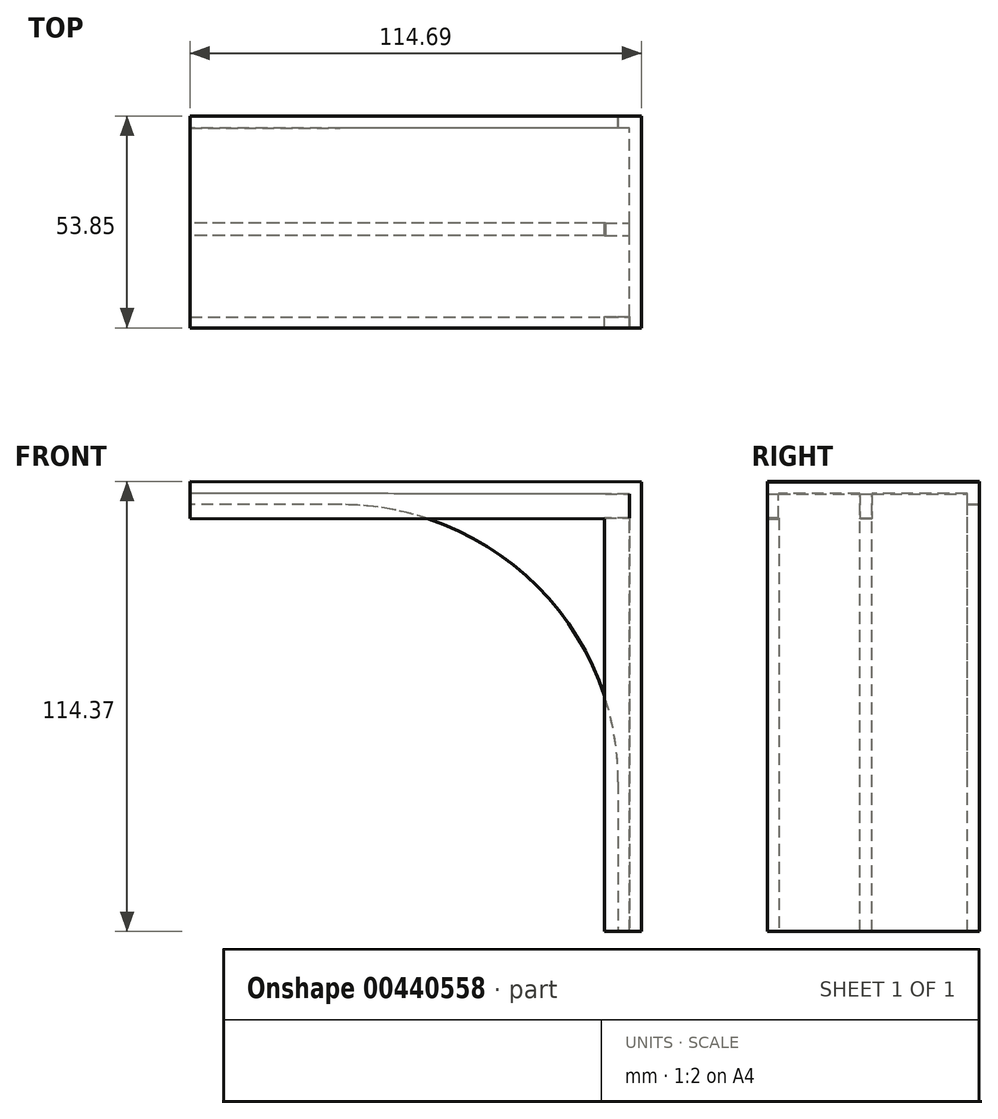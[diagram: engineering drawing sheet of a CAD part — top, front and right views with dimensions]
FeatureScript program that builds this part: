
annotation { "Feature Type Name" : "Feature", "Feature Type Description" : "" }
export const myFeature = defineFeature(function(context is Context, id is Id, definition is map)
    precondition{}
    {
        {
            var Q0;
            Q0=qCreatedBy(makeId("Front.planeOp"),FACE);
            var sketch = newSketch(context, id + "F0", { "sketchPlane" : qUnion([Q0])});
            skLineSegment(sketch, "E0", {"start": v(-76.07, 76.33) * mm, "end": v(76.59, -75.81) * mm});
            skLineSegment(sketch, "E1", {"start": v(76.59, -75.81) * mm, "end": v(76.59, 76.07) * mm});
            skLineSegment(sketch, "E2", {"start": v(76.59, 76.07) * mm, "end": v(-76.07, 76.33) * mm});
            skLineSegment(sketch, "E3.0", {"start": v(73.54, 73.03) * mm, "end": v(-76.08, 73.28) * mm});
            skLineSegment(sketch, "E3.1", {"start": v(73.54, -75.81) * mm, "end": v(73.54, 73.03) * mm});
            skSolve(sketch);
        }
        {
            var Q0;
            {var subQ1=sQuery(id+"F0.wireOp",EDGE,"E1");Q0=makeQuery(id+"F0.imprint","IMPRINT",FACE,{"disambiguationData":[TD([[makeQuery(id+"F0.imprint","IMPRINT",EDGE,{"derivedFrom":subQ1}),1.0]])]});}
            extrude(context, id + "F1", {"entities" : qUnion([Q0]), "depth" : 38.1 * mm});
        }
        {
            var Q0;
            {var subQ0=sQuery(id+"F0.wireOp",EDGE,"E3.0");var subQ1=sQuery(id+"F0.wireOp",EDGE,"E0");var subQ2=makeQuery(id+"F0.imprint","INTERSECT",VERTEX,{"derivedFrom":[subQ1,subQ0]});Q0=makeQuery(id+"F0.imprint","IMPRINT",FACE,{"disambiguationData":[TD([[makeQuery(id+"F0.imprint","IMPRINT",EDGE,{"disambiguationData":[TD([[subQ2,-1.0]])],"derivedFrom":subQ1}),1.0]])]});}
            extrude(context, id + "F2", {"entities" : qUnion([Q0]), "operationType" : NewBodyOperationType.ADD, "depth" : 3.05 * mm});
        }
        {
            var Q0;
            {var subQ0=sQuery(id+"F0.wireOp",EDGE,"E3.1");var subQ1=sQuery(id+"F0.wireOp",EDGE,"E3.0");var subQ2=sQuery(id+"F0.wireOp",EDGE,"E0");Q0=makeQuery(id+"F2.boolean.opBoolean","MERGE",FACE,{"derivedFrom":[makeQuery(id+"F1.opExtrude","CAP_FACE",FACE,{"disambiguationData":[OSD([subQ2,sQuery(id+"F0.wireOp",EDGE,"E1"),sQuery(id+"F0.wireOp",EDGE,"E2"),subQ1,subQ0])],"isStart":true}),makeQuery(id+"F2.opExtrude","CAP_FACE",FACE,{"disambiguationData":[OSD([subQ2,subQ1,subQ0])],"isStart":true})]});}
            var sketch = newSketch(context, id + "F3", { "sketchPlane" : qUnion([Q0])});
            skCircle(sketch, "E4", {"center": v(-0.25, -0.06) * mm, "radius": 70.41 * mm});
            skLineSegment(sketch, "E5", {"start": v(-70.92, -0.06) * mm, "end": v(-70.92, -76.52) * mm});
            skLineSegment(sketch, "E6", {"start": v(-70.92, -76.52) * mm, "end": v(75.56, -76.52) * mm});
            skLineSegment(sketch, "E7", {"start": v(75.56, -76.52) * mm, "end": v(75.56, 66.34) * mm});
            skLineSegment(sketch, "E8", {"start": v(75.56, 66.34) * mm, "end": v(75.9, 70.63) * mm});
            skLineSegment(sketch, "E9", {"start": v(75.9, 70.63) * mm, "end": v(0, 70.35) * mm});
            skSolve(sketch);
        }
        {
            var Q0;
            {var subQ0=sQuery(id+"F3.wireOp",EDGE,"E4");var subQ1=sQuery(id+"F0.wireOp",EDGE,"E0");var subQ2=makeQuery(id+"F2.boolean.opBoolean","MERGE",EDGE,{"derivedFrom":[makeQuery(id+"F1.opExtrude","CAP_EDGE",EDGE,{"disambiguationData":[OSD([subQ1]),TDD([makeQuery(id+"F0.imprint","IMPRINT",EDGE,{"disambiguationData":[TD([[makeQuery(id+"F0.imprint","INTERSECT",VERTEX,{"derivedFrom":[subQ1,sQuery(id+"F0.wireOp",EDGE,"E2")]}),-1.0]])],"derivedFrom":subQ1})])],"isStart":true}),makeQuery(id+"F1.opExtrude","CAP_EDGE",EDGE,{"disambiguationData":[OSD([subQ1]),TDD([makeQuery(id+"F0.imprint","IMPRINT",EDGE,{"disambiguationData":[TD([[makeQuery(id+"F0.imprint","INTERSECT",VERTEX,{"derivedFrom":[subQ1,sQuery(id+"F0.wireOp",EDGE,"E1")]}),1.0]])],"derivedFrom":subQ1})])],"isStart":true}),makeQuery(id+"F2.opExtrude","CAP_EDGE",EDGE,{"disambiguationData":[OSD([subQ1])],"isStart":true})]});var subQ3=makeQuery(id+"F3.imprint","INTERSECT",VERTEX,{"disambiguationData":[OD(0.0)],"derivedFrom":[subQ2,subQ0]});Q0=makeQuery(id+"F3.imprint","IMPRINT",FACE,{"disambiguationData":[TD([[makeQuery(id+"F3.imprint","IMPRINT",EDGE,{"disambiguationData":[TD([[subQ3,1.0]])],"derivedFrom":subQ0}),1.0]])]});}
            extrude(context, id + "F4", {"entities" : qUnion([Q0]), "operationType" : NewBodyOperationType.REMOVE, "oppositeDirection" : true, "depth" : 25.4 * mm});
        }
        {
            var Q0;
            {var subQ0=sQuery(id+"F0.wireOp",EDGE,"E3.1");var subQ1=sQuery(id+"F0.wireOp",EDGE,"E3.0");var subQ2=sQuery(id+"F0.wireOp",EDGE,"E0");Q0=makeQuery(id+"F2.boolean.opBoolean","MERGE",FACE,{"derivedFrom":[makeQuery(id+"F1.opExtrude","CAP_FACE",FACE,{"disambiguationData":[OSD([subQ2,sQuery(id+"F0.wireOp",EDGE,"E1"),sQuery(id+"F0.wireOp",EDGE,"E2"),subQ1,subQ0])],"isStart":true}),makeQuery(id+"F2.opExtrude","CAP_FACE",FACE,{"disambiguationData":[OSD([subQ2,subQ1,subQ0])],"isStart":true})]});}
            var sketch = newSketch(context, id + "F5", { "sketchPlane" : qUnion([Q0])});
            skLineSegment(sketch, "E10", {"start": v(-70.67, 0) * mm, "end": v(-70.67, -72.33) * mm});
            skLineSegment(sketch, "E11", {"start": v(-70.67, -72.33) * mm, "end": v(-36.55, -64.83) * mm});
            skLineSegment(sketch, "E12", {"start": v(-36.55, -64.83) * mm, "end": v(-70.67, 0) * mm});
            skLineSegment(sketch, "E13", {"start": v(0, 70.35) * mm, "end": v(70.07, 70.35) * mm});
            skLineSegment(sketch, "E14", {"start": v(70.07, 70.35) * mm, "end": v(70.07, 29.53) * mm});
            skLineSegment(sketch, "E15", {"start": v(70.07, 29.53) * mm, "end": v(0, 70.35) * mm});
            skSolve(sketch);
        }
        {
            var Q0;
            {var subQ0=sQuery(id+"F5.wireOp",EDGE,"E10");var subQ1=sQuery(id+"F3.wireOp",EDGE,"E4");var subQ2=makeQuery(id+"F4.boolean.opBoolean","COPY",EDGE,{"derivedFrom":makeQuery(id+"F4.opExtrude","CAP_EDGE",EDGE,{"disambiguationData":[OSD([subQ1])],"isStart":true})});var subQ3=makeQuery(id+"F5.imprint","INTERSECT",VERTEX,{"derivedFrom":[subQ2,subQ0]});Q0=makeQuery(id+"F5.imprint","IMPRINT",FACE,{"disambiguationData":[TD([[makeQuery(id+"F5.imprint","IMPRINT",EDGE,{"disambiguationData":[TD([[subQ3,-1.0]])],"derivedFrom":subQ0}),1.0]])]});}
            var Q1;
            {var subQ0=sQuery(id+"F5.wireOp",EDGE,"E13");Q1=makeQuery(id+"F5.imprint","IMPRINT",FACE,{"disambiguationData":[TD([[makeQuery(id+"F5.imprint","IMPRINT",EDGE,{"derivedFrom":subQ0}),-1.0]])]});}
            extrude(context, id + "F6", {"entities" : qUnion([Q0, Q1]), "operationType" : NewBodyOperationType.REMOVE, "endBound" : BoundingType.THROUGH_ALL, "oppositeDirection" : true, "depth" : 25.4 * mm});
        }
        {
            var Q0;
            Q0=makeQuery(id+"F1.opExtrude","SWEPT_FACE",FACE,{"disambiguationData":[OSD([sQuery(id+"F0.wireOp",EDGE,"E3.1")])]});
            var sketch = newSketch(context, id + "F7", { "sketchPlane" : qUnion([Q0])});
            skLineSegment(sketch, "E16.bottom", {"start": v(27.25, -72.77) * mm, "end": v(30.39, -72.77) * mm});
            skLineSegment(sketch, "E16.top", {"start": v(27.25, 73.03) * mm, "end": v(30.39, 73.03) * mm});
            skLineSegment(sketch, "E16.left", {"start": v(27.25, -72.77) * mm, "end": v(27.25, 73.03) * mm});
            skLineSegment(sketch, "E16.right", {"start": v(30.39, -72.77) * mm, "end": v(30.39, 73.03) * mm});
            skSolve(sketch);
        }
        {
            var Q0;
            Q0 = qSketchRegion(id + "F7", true);
            extrude(context, id + "F8", {"entities" : qUnion([Q0]), "operationType" : NewBodyOperationType.ADD, "depth" : 6.35 * mm});
        }
        {
            var Q0;
            Q0=makeQuery(id+"F1.opExtrude","SWEPT_FACE",FACE,{"disambiguationData":[OSD([sQuery(id+"F0.wireOp",EDGE,"E3.0")])]});
            var sketch = newSketch(context, id + "F9", { "sketchPlane" : qUnion([Q0])});
            skLineSegment(sketch, "E17.bottom", {"start": v(67.26, 30.39) * mm, "end": v(-73.13, 30.39) * mm});
            skLineSegment(sketch, "E17.top", {"start": v(67.26, 27.25) * mm, "end": v(-73.13, 27.25) * mm});
            skLineSegment(sketch, "E17.left", {"start": v(67.26, 30.39) * mm, "end": v(67.26, 27.25) * mm});
            skLineSegment(sketch, "E17.right", {"start": v(-73.13, 30.39) * mm, "end": v(-73.13, 27.25) * mm});
            skSolve(sketch);
        }
        {
            var Q0;
            Q0 = qSketchRegion(id + "F9", true);
            extrude(context, id + "F10", {"entities" : qUnion([Q0]), "operationType" : NewBodyOperationType.ADD, "depth" : 6.35 * mm});
        }
        {
            var Q0;
            Q0=makeQuery(id+"F10.opExtrude","CAP_EDGE",EDGE,{"disambiguationData":[OSD([sQuery(id+"F9.wireOp",EDGE,"E17.right")])],"isStart":false});
            chamfer(context, id + "F11", {"entities" : qUnion([Q0]), "width" : 5.08 * mm, "tangentPropagation" : true});
        }
        {
            var Q0;
            Q0=makeQuery(id+"F8.opExtrude","CAP_EDGE",EDGE,{"disambiguationData":[OSD([sQuery(id+"F7.wireOp",EDGE,"E16.bottom")])],"isStart":false});
            chamfer(context, id + "F12", {"entities" : qUnion([Q0]), "width" : 5.08 * mm, "tangentPropagation" : true});
        }
        {
            var Q0;
            Q0=makeQuery(id+"F1.opExtrude","CAP_FACE",FACE,{"disambiguationData":[OSD([sQuery(id+"F0.wireOp",EDGE,"E0"),sQuery(id+"F0.wireOp",EDGE,"E1"),sQuery(id+"F0.wireOp",EDGE,"E2"),sQuery(id+"F0.wireOp",EDGE,"E3.0"),sQuery(id+"F0.wireOp",EDGE,"E3.1")])],"isStart":false});
            extrude(context, id + "F13", {"entities" : qUnion([Q0]), "operationType" : NewBodyOperationType.ADD, "depth" : 15.75 * mm});
        }
        {
            var Q0;
            {var subQ0=sQuery(id+"F0.wireOp",EDGE,"E3.0");Q0=makeQuery(id+"F13.boolean.opBoolean","MERGE",FACE,{"derivedFrom":[makeQuery(id+"F1.opExtrude","SWEPT_FACE",FACE,{"disambiguationData":[OSD([subQ0])]}),makeQuery(id+"F13.opExtrude","SWEPT_FACE",FACE,{"disambiguationData":[OSD([subQ0])]})]});}
            var sketch = newSketch(context, id + "F14", { "sketchPlane" : qUnion([Q0])});
            skLineSegment(sketch, "E18.bottom", {"start": v(-73.13, 51.03) * mm, "end": v(73.42, 51.03) * mm});
            skLineSegment(sketch, "E18.top", {"start": v(-73.13, 53.85) * mm, "end": v(73.42, 53.85) * mm});
            skLineSegment(sketch, "E18.left", {"start": v(-73.13, 51.03) * mm, "end": v(-73.13, 53.85) * mm});
            skLineSegment(sketch, "E18.right", {"start": v(73.42, 51.03) * mm, "end": v(73.42, 53.85) * mm});
            skSolve(sketch);
        }
        {
            var Q0;
            Q0 = qSketchRegion(id + "F14", true);
            extrude(context, id + "F15", {"entities" : qUnion([Q0]), "operationType" : NewBodyOperationType.ADD, "depth" : 6.35 * mm});
        }
        {
            var Q0;
            Q0=makeQuery(id+"F15.opExtrude","CAP_EDGE",EDGE,{"disambiguationData":[OSD([sQuery(id+"F14.wireOp",EDGE,"E18.left")])],"isStart":false});
            chamfer(context, id + "F16", {"entities" : qUnion([Q0]), "width" : 5.08 * mm, "tangentPropagation" : true});
        }
        {
            var Q0;
            {var subQ0=sQuery(id+"F0.wireOp",EDGE,"E3.1");Q0=makeQuery(id+"F13.boolean.opBoolean","MERGE",FACE,{"derivedFrom":[makeQuery(id+"F8.boolean.opBoolean","SPLIT",FACE,{"disambiguationData":[TD([makeQuery(id+"F8.opExtrude","SWEPT_FACE",FACE,{"disambiguationData":[OSD([sQuery(id+"F7.wireOp",EDGE,"E16.right")])]})])],"derivedFrom":makeQuery(id+"F1.opExtrude","SWEPT_FACE",FACE,{"disambiguationData":[OSD([subQ0])]})}),makeQuery(id+"F13.opExtrude","SWEPT_FACE",FACE,{"disambiguationData":[OSD([subQ0])]})]});}
            var sketch = newSketch(context, id + "F17", { "sketchPlane" : qUnion([Q0])});
            skLineSegment(sketch, "E19.bottom", {"start": v(50.95, 66.97) * mm, "end": v(53.85, 66.97) * mm});
            skLineSegment(sketch, "E19.top", {"start": v(50.95, -72.77) * mm, "end": v(53.85, -72.77) * mm});
            skLineSegment(sketch, "E19.left", {"start": v(50.95, 66.97) * mm, "end": v(50.95, -72.77) * mm});
            skLineSegment(sketch, "E19.right", {"start": v(53.85, 66.97) * mm, "end": v(53.85, -72.77) * mm});
            skSolve(sketch);
        }
        {
            var Q0;
            Q0 = qSketchRegion(id + "F17", true);
            extrude(context, id + "F18", {"entities" : qUnion([Q0]), "operationType" : NewBodyOperationType.ADD, "depth" : 6.35 * mm});
        }
        {
            var Q0;
            Q0=makeQuery(id+"F18.opExtrude","CAP_EDGE",EDGE,{"disambiguationData":[OSD([sQuery(id+"F17.wireOp",EDGE,"E19.top")])],"isStart":false});
            chamfer(context, id + "F19", {"entities" : qUnion([Q0]), "width" : 5.08 * mm, "tangentPropagation" : true});
        }
        {
            var Q0;
            Q0=qCreatedBy(makeId("Front.planeOp"),FACE);
            var sketch = newSketch(context, id + "F20", { "sketchPlane" : qUnion([Q0])});
            skLineSegment(sketch, "E20", {"start": v(-91.16, 83.67) * mm, "end": v(-38.1, 83.67) * mm});
            skLineSegment(sketch, "E21", {"start": v(-38.1, 83.67) * mm, "end": v(-38.1, -38.1) * mm});
            skLineSegment(sketch, "E22", {"start": v(-38.1, -38.1) * mm, "end": v(81.37, -38.1) * mm});
            skLineSegment(sketch, "E23", {"start": v(81.37, -38.1) * mm, "end": v(81.37, -82.57) * mm});
            skLineSegment(sketch, "E24", {"start": v(81.37, -82.57) * mm, "end": v(-93.7, -82.57) * mm});
            skLineSegment(sketch, "E25", {"start": v(-93.7, -82.57) * mm, "end": v(-90.71, 84.1) * mm});
            skSolve(sketch);
        }
        {
            var Q0;
            Q0 = qSketchRegion(id + "F20", true);
            extrude(context, id + "F21", {"entities" : qUnion([Q0]), "operationType" : NewBodyOperationType.REMOVE, "endBound" : BoundingType.THROUGH_ALL, "depth" : 25.4 * mm});
        }
    });
